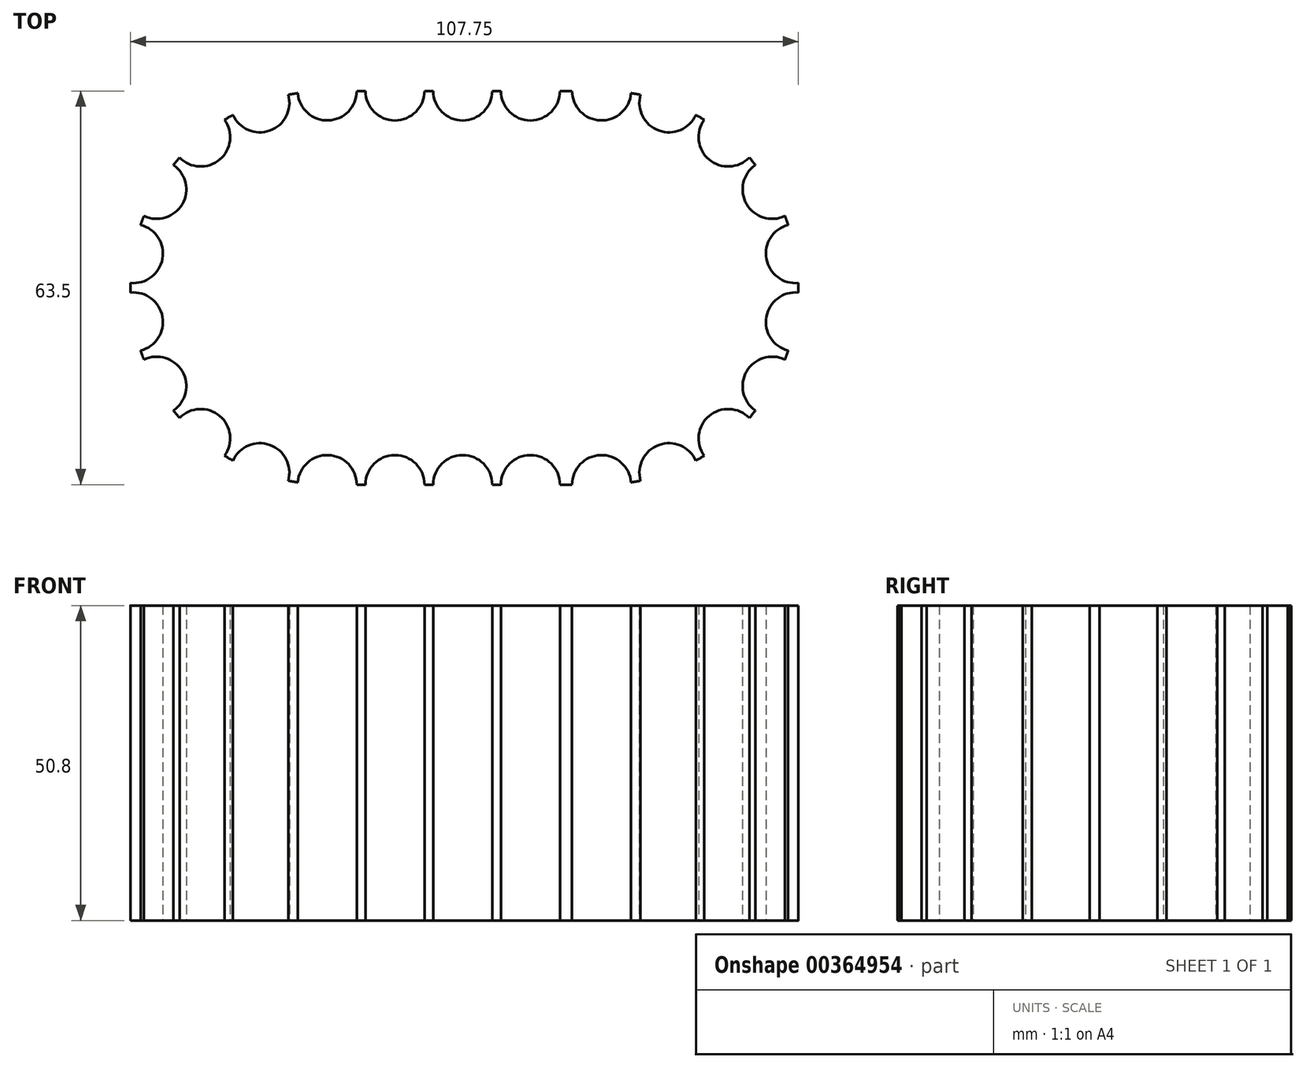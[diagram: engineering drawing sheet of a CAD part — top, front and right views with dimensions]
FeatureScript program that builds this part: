
annotation { "Feature Type Name" : "Feature", "Feature Type Description" : "" }
export const myFeature = defineFeature(function(context is Context, id is Id, definition is map)
    precondition{}
    {
        {
            var Q0;
            Q0=qCreatedBy(makeId("Top.planeOp"),FACE);
            var sketch = newSketch(context, id + "F0", { "sketchPlane" : qUnion([Q0])});
            skLineSegment(sketch, "E0", {"start": v(0, 0) * mm, "end": v(-44.25, 0) * mm, "construction": true});
            skArc(sketch, "E1", {"start": v(-44.25, 31.75) * mm, "mid": v(-76, 0) * mm, "end": v(-44.25, -31.75) * mm});
            skArc(sketch, "E2", {"start": v(0, -31.75) * mm, "mid": v(31.75, 0) * mm, "end": v(0, 31.75) * mm});
            skLineSegment(sketch, "E3", {"start": v(0, 31.75) * mm, "end": v(-44.25, 31.75) * mm});
            skLineSegment(sketch, "E4", {"start": v(0, -31.75) * mm, "end": v(-44.25, -31.75) * mm});
            skCircle(sketch, "E5", {"center": v(0, 31.75) * mm, "radius": 4.76 * mm});
            skCircle(sketch, "E6", {"center": v(-44.25, 31.75) * mm, "radius": 4.76 * mm});
            skCircle(sketch, "E7.1.0", {"center": v(10.86, 29.84) * mm, "radius": 4.76 * mm});
            skCircle(sketch, "E7.2.0", {"center": v(20.4, 24.32) * mm, "radius": 4.76 * mm});
            skCircle(sketch, "E7.3.0", {"center": v(27.5, 15.87) * mm, "radius": 4.76 * mm});
            skCircle(sketch, "E7.4.0", {"center": v(31.27, 5.51) * mm, "radius": 4.76 * mm});
            skCircle(sketch, "E7.5.0", {"center": v(31.27, -5.51) * mm, "radius": 4.76 * mm});
            skCircle(sketch, "E7.6.0", {"center": v(27.5, -15.88) * mm, "radius": 4.76 * mm});
            skCircle(sketch, "E7.7.0", {"center": v(20.4, -24.32) * mm, "radius": 4.76 * mm});
            skCircle(sketch, "E7.8.0", {"center": v(10.86, -29.84) * mm, "radius": 4.76 * mm});
            skCircle(sketch, "E7.9.0", {"center": v(0, -31.75) * mm, "radius": 4.76 * mm});
            skLineSegment(sketch, "E7.anchor1", {"start": v(0, 0) * mm, "end": v(0, 31.75) * mm, "construction": true});
            skLineSegment(sketch, "E7.anchor2", {"start": v(0, 0) * mm, "end": v(0, -31.75) * mm, "construction": true});
            skLineSegment(sketch, "E8.anchor1", {"start": v(0, 0) * mm, "end": v(-44.25, 31.75) * mm, "construction": true});
            skLineSegment(sketch, "E8.anchor2", {"start": v(0, 0) * mm, "end": v(-38.95, -38.06) * mm, "construction": true});
            skCircle(sketch, "E9.1.0", {"center": v(-55.1, 29.84) * mm, "radius": 4.76 * mm});
            skCircle(sketch, "E9.2.0", {"center": v(-64.66, 24.32) * mm, "radius": 4.76 * mm});
            skCircle(sketch, "E9.3.0", {"center": v(-71.74, 15.87) * mm, "radius": 4.76 * mm});
            skCircle(sketch, "E9.4.0", {"center": v(-75.51, 5.51) * mm, "radius": 4.76 * mm});
            skCircle(sketch, "E9.5.0", {"center": v(-75.51, -5.51) * mm, "radius": 4.76 * mm});
            skCircle(sketch, "E9.6.0", {"center": v(-71.74, -15.87) * mm, "radius": 4.76 * mm});
            skCircle(sketch, "E9.7.0", {"center": v(-64.66, -24.32) * mm, "radius": 4.76 * mm});
            skCircle(sketch, "E9.8.0", {"center": v(-55.1, -29.84) * mm, "radius": 4.76 * mm});
            skCircle(sketch, "E9.9.0", {"center": v(-44.25, -31.75) * mm, "radius": 4.76 * mm});
            skLineSegment(sketch, "E9.anchor1", {"start": v(-44.25, 0) * mm, "end": v(-44.25, 31.75) * mm, "construction": true});
            skLineSegment(sketch, "E9.anchor2", {"start": v(-44.25, 0) * mm, "end": v(-44.25, -31.75) * mm, "construction": true});
            skCircle(sketch, "E10.1.0.0", {"center": v(-33.32, -31.75) * mm, "radius": 4.76 * mm});
            skCircle(sketch, "E10.2.0.0", {"center": v(-22.4, -31.75) * mm, "radius": 4.76 * mm});
            skCircle(sketch, "E10.3.0.0", {"center": v(-11.48, -31.75) * mm, "radius": 4.76 * mm});
            skLineSegment(sketch, "E10.direction1", {"start": v(-44.25, -31.75) * mm, "end": v(-33.32, -31.75) * mm, "construction": true});
            skCircle(sketch, "E11.1.0.0", {"center": v(-33.32, 31.75) * mm, "radius": 4.76 * mm});
            skCircle(sketch, "E11.2.0.0", {"center": v(-22.4, 31.75) * mm, "radius": 4.76 * mm});
            skCircle(sketch, "E11.3.0.0", {"center": v(-11.48, 31.75) * mm, "radius": 4.76 * mm});
            skLineSegment(sketch, "E11.direction1", {"start": v(-44.25, 31.75) * mm, "end": v(-33.32, 31.75) * mm, "construction": true});
            skSolve(sketch);
        }
        {
            var Q0;
            {var subQ1=sQuery(id+"F0.wireOp",EDGE,"E1");var subQ33=sQuery(id+"F0.wireOp",EDGE,"E6");var subQ34=makeQuery(id+"F0.imprint","INTERSECT",VERTEX,{"derivedFrom":[subQ1,subQ33]});Q0=makeQuery(id+"F0.imprint","IMPRINT",FACE,{"disambiguationData":[TD([[makeQuery(id+"F0.imprint","IMPRINT",EDGE,{"disambiguationData":[TD([[subQ34,-1.0]])],"derivedFrom":subQ1}),1.0]])]});}
            extrude(context, id + "F1", {"entities" : qUnion([Q0]), "depth" : 50.8 * mm});
        }
    });
